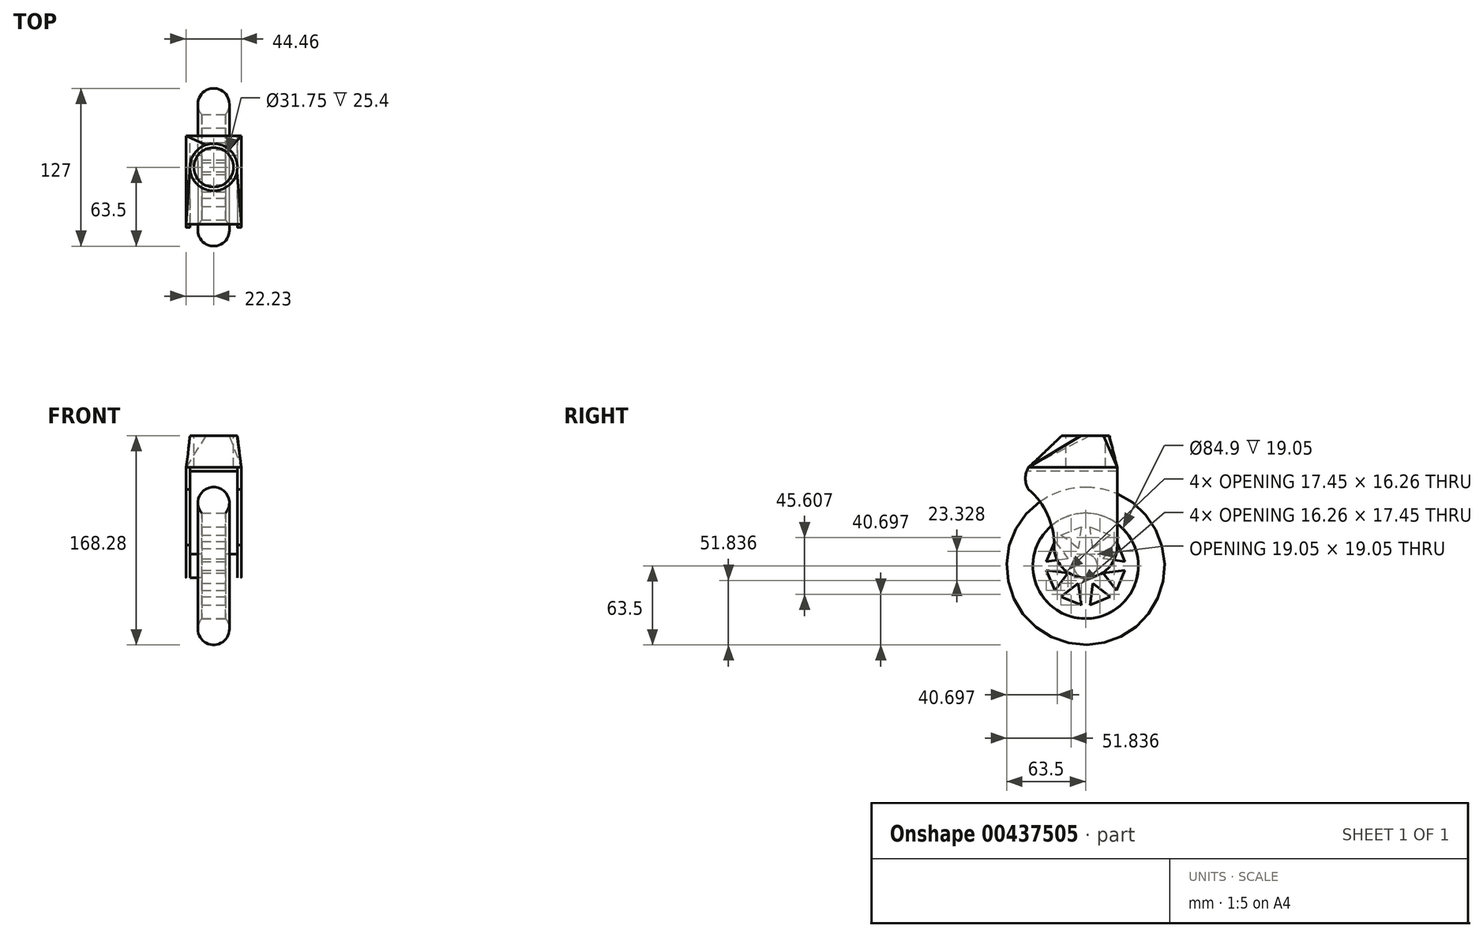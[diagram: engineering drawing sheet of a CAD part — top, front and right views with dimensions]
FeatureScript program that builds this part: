
annotation { "Feature Type Name" : "Feature", "Feature Type Description" : "" }
export const myFeature = defineFeature(function(context is Context, id is Id, definition is map)
    precondition{}
    {
        {
            var Q0;
            Q0=qCreatedBy(makeId("Top.planeOp"),FACE);
            var sketch = newSketch(context, id + "F0", { "sketchPlane" : qUnion([Q0])});
            skLineSegment(sketch, "E0", {"start": v(-9.52, -42.4) * mm, "end": v(-9.52, 0) * mm});
            skLineSegment(sketch, "E1", {"start": v(-9.52, 0) * mm, "end": v(9.52, 0) * mm});
            skLineSegment(sketch, "E2", {"start": v(9.52, 0) * mm, "end": v(9.52, -42.4) * mm});
            skArc(sketch, "E3", {"start": v(-9.53, -42.4) * mm, "mid": v(0, -63.5) * mm, "end": v(9.53, -42.4) * mm});
            skSolve(sketch);
        }
        {
            var Q0;
            Q0 = qSketchRegion(id + "F0", true);
            var Q1;
            Q1=sQuery(id+"F0.wireOp",EDGE,"E1");
            revolve(context, id + "F1", {"surfaceOperationType" : NewSurfaceOperationType.NEW, "entities" : qUnion([Q0]), "axis" : qUnion([Q1]), "revolveType" : RevolveType.FULL});
        }
        {
            var Q0;
            Q0=makeQuery(id+"F1.opRevolve","SWEPT_FACE",FACE,{"disambiguationData":[OSD([sQuery(id+"F0.wireOp",EDGE,"E2")])]});
            var sketch = newSketch(context, id + "F2", { "sketchPlane" : qUnion([Q0])});
            skCircle(sketch, "E4", {"center": v(0, 0) * mm, "radius": 42.45 * mm});
            skLineSegment(sketch, "E5", {"start": v(0, 0) * mm, "end": v(42.4, 0) * mm});
            skLineSegment(sketch, "E6", {"start": v(0, 0) * mm, "end": v(0, 42.4) * mm});
            skLineSegment(sketch, "E7", {"start": v(0, 0) * mm, "end": v(26.99, 26.99) * mm});
            skLineSegment(sketch, "E8", {"start": v(0, 0) * mm, "end": v(9.72, 23.47) * mm});
            skCircle(sketch, "E9.cCircle", {"center": v(9.72, 23.47) * mm, "radius": 5.08 * mm, "construction": true});
            skLineSegment(sketch, "E9.0", {"start": v(3.54, 31.53) * mm, "end": v(19.8, 24.8) * mm});
            skLineSegment(sketch, "E9.1", {"start": v(19.8, 24.8) * mm, "end": v(5.83, 14.08) * mm});
            skLineSegment(sketch, "E9.2", {"start": v(5.83, 14.08) * mm, "end": v(3.54, 31.53) * mm});
            skPoint(sketch, "E9.0.midPoint", {"position": v(11.66, 28.16) * mm});
            skLineSegment(sketch, "E10.1.0", {"start": v(-3.54, 31.53) * mm, "end": v(-5.83, 14.08) * mm});
            skLineSegment(sketch, "E10.1.1", {"start": v(-5.83, 14.08) * mm, "end": v(-19.8, 24.8) * mm});
            skLineSegment(sketch, "E10.1.2", {"start": v(-19.8, 24.8) * mm, "end": v(-3.54, 31.53) * mm});
            skLineSegment(sketch, "E10.2.0", {"start": v(-24.8, 19.8) * mm, "end": v(-14.08, 5.83) * mm});
            skLineSegment(sketch, "E10.2.1", {"start": v(-14.08, 5.83) * mm, "end": v(-31.53, 3.54) * mm});
            skLineSegment(sketch, "E10.2.2", {"start": v(-31.53, 3.54) * mm, "end": v(-24.8, 19.8) * mm});
            skLineSegment(sketch, "E10.3.0", {"start": v(-31.53, -3.54) * mm, "end": v(-14.08, -5.83) * mm});
            skLineSegment(sketch, "E10.3.1", {"start": v(-14.08, -5.83) * mm, "end": v(-24.8, -19.8) * mm});
            skLineSegment(sketch, "E10.3.2", {"start": v(-24.8, -19.8) * mm, "end": v(-31.53, -3.54) * mm});
            skLineSegment(sketch, "E10.4.0", {"start": v(-19.8, -24.8) * mm, "end": v(-5.83, -14.08) * mm});
            skLineSegment(sketch, "E10.4.1", {"start": v(-5.83, -14.08) * mm, "end": v(-3.54, -31.53) * mm});
            skLineSegment(sketch, "E10.4.2", {"start": v(-3.54, -31.53) * mm, "end": v(-19.8, -24.8) * mm});
            skLineSegment(sketch, "E10.5.0", {"start": v(3.54, -31.53) * mm, "end": v(5.83, -14.08) * mm});
            skLineSegment(sketch, "E10.5.1", {"start": v(5.83, -14.08) * mm, "end": v(19.8, -24.8) * mm});
            skLineSegment(sketch, "E10.5.2", {"start": v(19.8, -24.8) * mm, "end": v(3.54, -31.53) * mm});
            skLineSegment(sketch, "E10.6.0", {"start": v(24.8, -19.8) * mm, "end": v(14.08, -5.83) * mm});
            skLineSegment(sketch, "E10.6.1", {"start": v(14.08, -5.83) * mm, "end": v(31.53, -3.54) * mm});
            skLineSegment(sketch, "E10.6.2", {"start": v(31.53, -3.54) * mm, "end": v(24.8, -19.8) * mm});
            skLineSegment(sketch, "E10.7.0", {"start": v(31.53, 3.54) * mm, "end": v(14.08, 5.83) * mm});
            skLineSegment(sketch, "E10.7.1", {"start": v(14.08, 5.83) * mm, "end": v(24.8, 19.8) * mm});
            skLineSegment(sketch, "E10.7.2", {"start": v(24.8, 19.8) * mm, "end": v(31.53, 3.54) * mm});
            skSolve(sketch);
        }
        {
            var Q0;
            Q0=makeQuery(id+"F2.imprint","IMPRINT",FACE,{"disambiguationData":[TD([[makeQuery(id+"F2.imprint","IMPRINT",EDGE,{"derivedFrom":sQuery(id+"F2.wireOp",EDGE,"E4")}),1.0]])]});
            var Q1;
            Q1=makeQuery(id+"F2.imprint","IMPRINT",FACE,{"disambiguationData":[TD([[makeQuery(id+"F2.imprint","IMPRINT",EDGE,{"derivedFrom":sQuery(id+"F2.wireOp",EDGE,"E10.1.0")}),-1.0]])]});
            var Q2;
            Q2=makeQuery(id+"F2.imprint","IMPRINT",FACE,{"disambiguationData":[TD([[makeQuery(id+"F2.imprint","IMPRINT",EDGE,{"derivedFrom":sQuery(id+"F2.wireOp",EDGE,"E9.0")}),-1.0]])]});
            var Q3;
            Q3=makeQuery(id+"F2.imprint","IMPRINT",FACE,{"disambiguationData":[TD([[makeQuery(id+"F2.imprint","IMPRINT",EDGE,{"derivedFrom":sQuery(id+"F2.wireOp",EDGE,"E10.7.0")}),-1.0]])]});
            var Q4;
            Q4=makeQuery(id+"F2.imprint","IMPRINT",FACE,{"disambiguationData":[TD([[makeQuery(id+"F2.imprint","IMPRINT",EDGE,{"derivedFrom":sQuery(id+"F2.wireOp",EDGE,"E10.6.0")}),-1.0]])]});
            var Q5;
            Q5=makeQuery(id+"F2.imprint","IMPRINT",FACE,{"disambiguationData":[TD([[makeQuery(id+"F2.imprint","IMPRINT",EDGE,{"derivedFrom":sQuery(id+"F2.wireOp",EDGE,"E10.5.0")}),-1.0]])]});
            var Q6;
            Q6=makeQuery(id+"F2.imprint","IMPRINT",FACE,{"disambiguationData":[TD([[makeQuery(id+"F2.imprint","IMPRINT",EDGE,{"derivedFrom":sQuery(id+"F2.wireOp",EDGE,"E10.4.0")}),-1.0]])]});
            var Q7;
            Q7=makeQuery(id+"F2.imprint","IMPRINT",FACE,{"disambiguationData":[TD([[makeQuery(id+"F2.imprint","IMPRINT",EDGE,{"derivedFrom":sQuery(id+"F2.wireOp",EDGE,"E10.3.0")}),-1.0]])]});
            var Q8;
            Q8=makeQuery(id+"F2.imprint","IMPRINT",FACE,{"disambiguationData":[TD([[makeQuery(id+"F2.imprint","IMPRINT",EDGE,{"derivedFrom":sQuery(id+"F2.wireOp",EDGE,"E10.2.0")}),-1.0]])]});
            extrude(context, id + "F3", {"entities" : qUnion([Q0, Q1, Q2, Q3, Q4, Q5, Q6, Q7, Q8]), "operationType" : NewBodyOperationType.REMOVE, "oppositeDirection" : true, "depth" : 25.4 * mm, "offsetDistance" : 25.4 * mm});
        }
        {
            var Q0;
            Q0=qCreatedBy(makeId("Right.planeOp"),FACE);
            var sketch = newSketch(context, id + "F4", { "sketchPlane" : qUnion([Q0])});
            skCircle(sketch, "E11", {"center": v(0, 0) * mm, "radius": 9.53 * mm});
            skSolve(sketch);
        }
        {
            var Q0;
            Q0 = qSketchRegion(id + "F4", true);
            extrude(context, id + "F5", {"entities" : qUnion([Q0]), "operationType" : NewBodyOperationType.ADD, "depth" : 19.05 * mm, "offsetDistance" : 25.4 * mm, "hasSecondDirection" : true, "secondDirectionOppositeDirection" : true, "secondDirectionDepth" : 19.05 * mm});
        }
        {
            var Q0;
            Q0=makeQuery(id+"F5.opExtrude","CAP_FACE",FACE,{"disambiguationData":[OSD([sQuery(id+"F4.wireOp",EDGE,"E11")])],"isStart":false});
            var sketch = newSketch(context, id + "F6", { "sketchPlane" : qUnion([Q0])});
            skCircle(sketch, "E12", {"center": v(0, 15.88) * mm, "radius": 25.4 * mm});
            skArc(sketch, "E13", {"start": v(-25.4, 15.88) * mm, "mid": v(-30.45, 40.99) * mm, "end": v(-45.81, 61.49) * mm});
            skLineSegment(sketch, "E14", {"start": v(25.4, 15.88) * mm, "end": v(25.4, 61.49) * mm});
            skLineSegment(sketch, "E15", {"start": v(25.4, 15.88) * mm, "end": v(25.4, 79.38) * mm});
            skLineSegment(sketch, "E16", {"start": v(25.4, 79.38) * mm, "end": v(-45.81, 79.38) * mm});
            skArc(sketch, "E17", {"start": v(-45.81, 79.38) * mm, "mid": v(-48.37, 70.43) * mm, "end": v(-45.81, 61.49) * mm});
            skSolve(sketch);
        }
        {
            var Q0;
            Q0 = qSketchRegion(id + "F6", true);
            extrude(context, id + "F7", {"entities" : qUnion([Q0]), "operationType" : NewBodyOperationType.ADD, "depth" : 3.17 * mm, "offsetDistance" : 25.4 * mm});
        }
        {
            var Q0;
            Q0=makeQuery(id+"F3.boolean.opBoolean","SPLIT",BODY,{"disambiguationData":[OD(1.0)],"derivedFrom":makeQuery(id+"F1.opRevolve","SWEPT_BODY",BODY,{"disambiguationData":[OSD([sQuery(id+"F0.wireOp",EDGE,"E0"),sQuery(id+"F0.wireOp",EDGE,"E1"),sQuery(id+"F0.wireOp",EDGE,"E2"),sQuery(id+"F0.wireOp",EDGE,"E3")])]})});
            var Q1;
            Q1=qCreatedBy(makeId("Right.planeOp"),FACE);
            mirror(context, id + "F8", {"operationType" : NewBodyOperationType.ADD, "entities" : qUnion([Q0]), "mirrorPlane" : qUnion([Q1])});
        }
        {
            var Q0;
            Q0=makeQuery(id+"F8.opPattern","COPY",FACE,{"derivedFrom":makeQuery(id+"F7.opExtrude","SWEPT_FACE",FACE,{"disambiguationData":[OSD([sQuery(id+"F6.wireOp",EDGE,"E16")])]}),"instanceName":"1"});
            var sketch = newSketch(context, id + "F9", { "sketchPlane" : qUnion([Q0])});
            skLineSegment(sketch, "E18", {"start": v(-22.23, 25.4) * mm, "end": v(22.23, 25.4) * mm});
            skLineSegment(sketch, "E19", {"start": v(22.23, 25.4) * mm, "end": v(22.23, -45.81) * mm});
            skLineSegment(sketch, "E20", {"start": v(22.23, -45.81) * mm, "end": v(-22.23, -45.81) * mm});
            skLineSegment(sketch, "E21", {"start": v(-22.23, -45.81) * mm, "end": v(-22.23, 25.4) * mm});
            skSolve(sketch);
        }
        {
            var Q0;
            Q0 = qSketchRegion(id + "F9", true);
            extrude(context, id + "F10", {"entities" : qUnion([Q0]), "operationType" : NewBodyOperationType.ADD, "oppositeDirection" : true, "depth" : 3.17 * mm, "offsetDistance" : 25.4 * mm});
        }
        {
            var Q0;
            {var subQ0=makeQuery(id+"F7.opExtrude","SWEPT_FACE",FACE,{"disambiguationData":[OSD([sQuery(id+"F6.wireOp",EDGE,"E16")])]});Q0=makeQuery(id+"F10.boolean.opBoolean","MERGE",FACE,{"derivedFrom":[subQ0,makeQuery(id+"F8.opPattern","COPY",FACE,{"derivedFrom":subQ0,"instanceName":"1"}),makeQuery(id+"F10.opExtrude","CAP_FACE",FACE,{"disambiguationData":[OSD([sQuery(id+"F9.wireOp",EDGE,"E18"),sQuery(id+"F9.wireOp",EDGE,"E19"),sQuery(id+"F9.wireOp",EDGE,"E20"),sQuery(id+"F9.wireOp",EDGE,"E21")])],"isStart":true})]});}
            cPlane(context, id + "F11", {"entities" : qUnion([Q0]), "cplaneType" : CPlaneType.OFFSET, "offset" : 25.4 * mm, "width" : 152.4 * mm, "height" : 152.4 * mm});
        }
        {
            var Q0;
            Q0=qCreatedBy(id+"F11.planeOp",FACE);
            var sketch = newSketch(context, id + "F12", { "sketchPlane" : qUnion([Q0])});
            skCircle(sketch, "E22", {"center": v(0, 0) * mm, "radius": 19.05 * mm});
            skSolve(sketch);
        }
        {
            var Q1;
            Q1=makeQuery(id+"F12.imprint","IMPRINT",FACE,{"disambiguationData":[TD([[makeQuery(id+"F12.imprint","IMPRINT",EDGE,{"derivedFrom":sQuery(id+"F12.wireOp",EDGE,"E22")}),1.0]])]});
            var Q2;
            {var subQ0=makeQuery(id+"F7.opExtrude","SWEPT_FACE",FACE,{"disambiguationData":[OSD([sQuery(id+"F6.wireOp",EDGE,"E16")])]});Q2=makeQuery(id+"F10.boolean.opBoolean","MERGE",FACE,{"derivedFrom":[subQ0,makeQuery(id+"F8.opPattern","COPY",FACE,{"derivedFrom":subQ0,"instanceName":"1"}),makeQuery(id+"F10.opExtrude","CAP_FACE",FACE,{"disambiguationData":[OSD([sQuery(id+"F9.wireOp",EDGE,"E18"),sQuery(id+"F9.wireOp",EDGE,"E19"),sQuery(id+"F9.wireOp",EDGE,"E20"),sQuery(id+"F9.wireOp",EDGE,"E21")])],"isStart":true})]});}
            loft(context, id + "F13", {"operationType" : NewBodyOperationType.ADD, "sheetProfilesArray" : [{ "sheetProfileEntities" : qUnion([Q1]) }, { "sheetProfileEntities" : qUnion([Q2]) }]});
        }
        {
            var Q0;
            Q0=makeQuery(id+"F13.opLoft","CAP_FACE",FACE,{"disambiguationData":[OSD([makeQuery(id+"F12.imprint","IMPRINT",FACE,{"disambiguationData":[TD([[makeQuery(id+"F12.imprint","IMPRINT",EDGE,{"derivedFrom":sQuery(id+"F12.wireOp",EDGE,"E22")}),1.0]])]})])],"isStart":true});
            var sketch = newSketch(context, id + "F14", { "sketchPlane" : qUnion([Q0])});
            skCircle(sketch, "E23", {"center": v(0, 0) * mm, "radius": 15.88 * mm});
            skSolve(sketch);
        }
        {
            var Q0;
            Q0 = qSketchRegion(id + "F14", true);
            extrude(context, id + "F15", {"entities" : qUnion([Q0]), "operationType" : NewBodyOperationType.REMOVE, "oppositeDirection" : true, "depth" : 25.4 * mm, "offsetDistance" : 25.4 * mm});
        }
    });
